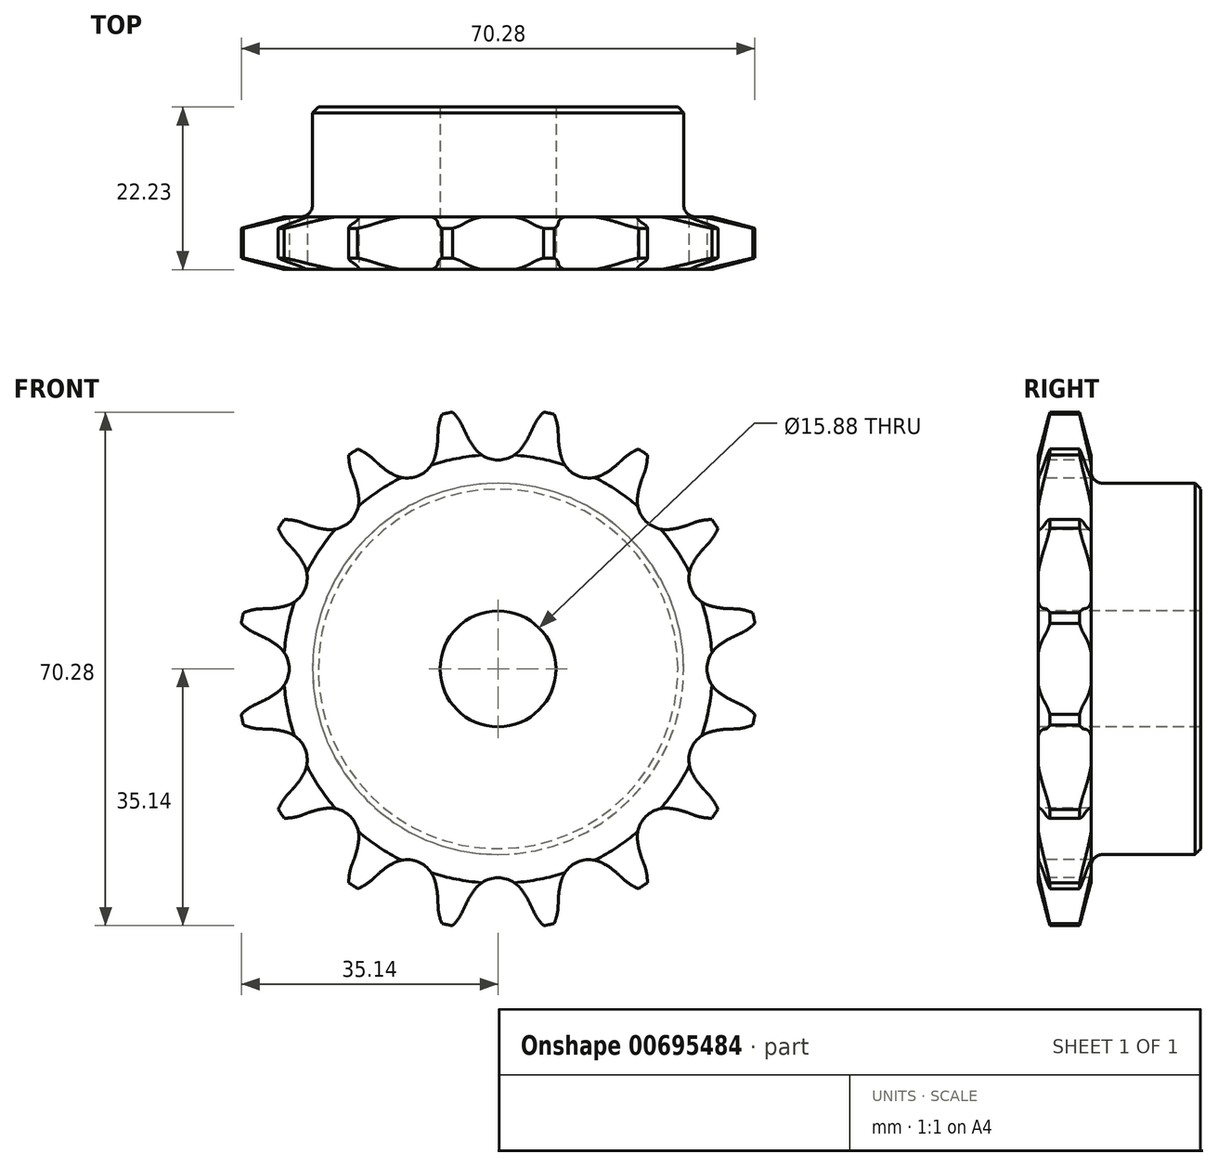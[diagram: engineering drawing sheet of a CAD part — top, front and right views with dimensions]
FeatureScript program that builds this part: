
annotation { "Feature Type Name" : "Feature", "Feature Type Description" : "" }
export const myFeature = defineFeature(function(context is Context, id is Id, definition is map)
    precondition{}
    {
        {
            var Q0;
            Q0=qCreatedBy(makeId("Right.planeOp"),FACE);
            var sketch = newSketch(context, id + "F0", { "sketchPlane" : qUnion([Q0])});
            skLineSegment(sketch, "E0", {"start": v(0, 0) * mm, "end": v(20.66, 0) * mm, "construction": true});
            skLineSegment(sketch, "E1.bottom", {"start": v(-1.57, 35.69) * mm, "end": v(5.65, 35.69) * mm});
            skLineSegment(sketch, "E1.top", {"start": v(-1.57, 7.94) * mm, "end": v(5.65, 7.94) * mm});
            skLineSegment(sketch, "E1.left", {"start": v(-1.57, 35.69) * mm, "end": v(-1.57, 7.94) * mm});
            skLineSegment(sketch, "E1.right", {"start": v(5.65, 35.69) * mm, "end": v(5.65, 7.94) * mm});
            skLineSegment(sketch, "E2.bottom", {"start": v(-1.57, 7.94) * mm, "end": v(20.66, 7.94) * mm});
            skLineSegment(sketch, "E2.top", {"start": v(-1.57, 25.4) * mm, "end": v(20.66, 25.4) * mm});
            skLineSegment(sketch, "E2.left", {"start": v(-1.57, 7.94) * mm, "end": v(-1.57, 25.4) * mm});
            skLineSegment(sketch, "E2.right", {"start": v(20.66, 7.94) * mm, "end": v(20.66, 25.4) * mm});
            skLineSegment(sketch, "E3.MirrorCS", {"start": v(-1.57, -7.94) * mm, "end": v(5.65, -7.94) * mm});
            skLineSegment(sketch, "E4.MirrorCS", {"start": v(20.66, -7.94) * mm, "end": v(20.66, -25.4) * mm});
            skLineSegment(sketch, "E5.MirrorCS", {"start": v(-1.57, -7.94) * mm, "end": v(20.66, -7.94) * mm});
            skLineSegment(sketch, "E6.MirrorCS", {"start": v(-1.57, -35.69) * mm, "end": v(5.65, -35.69) * mm});
            skLineSegment(sketch, "E7.MirrorCS", {"start": v(-1.57, -7.94) * mm, "end": v(-1.57, -25.4) * mm});
            skLineSegment(sketch, "E8.MirrorCS", {"start": v(-1.57, -25.4) * mm, "end": v(20.66, -25.4) * mm});
            skLineSegment(sketch, "E9.MirrorCS", {"start": v(5.65, -35.69) * mm, "end": v(5.65, -7.94) * mm});
            skLineSegment(sketch, "E10.MirrorCS", {"start": v(-1.57, -35.69) * mm, "end": v(-1.57, -7.94) * mm});
            skSolve(sketch);
        }
        {
            var Q0;
            {var subQ0=sQuery(id+"F0.wireOp",EDGE,"E1.bottom");Q0=makeQuery(id+"F0.imprint","IMPRINT",FACE,{"disambiguationData":[TD([[makeQuery(id+"F0.imprint","IMPRINT",EDGE,{"derivedFrom":subQ0}),-1.0]])]});}
            var Q1;
            {var subQ0=sQuery(id+"F0.wireOp",EDGE,"E1.top");Q1=makeQuery(id+"F0.imprint","IMPRINT",FACE,{"disambiguationData":[TD([[makeQuery(id+"F0.imprint","IMPRINT",EDGE,{"derivedFrom":subQ0}),1.0]])]});}
            var Q2;
            {var subQ0=sQuery(id+"F0.wireOp",EDGE,"E2.bottom");Q2=makeQuery(id+"F0.imprint","IMPRINT",FACE,{"disambiguationData":[TD([[makeQuery(id+"F0.imprint","IMPRINT",EDGE,{"derivedFrom":subQ0}),1.0]])]});}
            var Q3;
            Q3=sQuery(id+"F0.wireOp",EDGE,"E0");
            revolve(context, id + "F1", {"surfaceOperationType" : NewSurfaceOperationType.NEW, "entities" : qUnion([Q0, Q1, Q2]), "axis" : qUnion([Q3]), "revolveType" : RevolveType.FULL});
        }
        {
            var Q0;
            Q0=makeQuery(id+"F1.opRevolve","SWEPT_EDGE",EDGE,{"disambiguationData":[OSD([sQuery(id+"F0.wireOp",EDGE,"E1.right"),sQuery(id+"F0.wireOp",EDGE,"E2.top")])]});
            fillet(context, id + "F2", {"entities" : qUnion([Q0]), "tangentPropagation" : true, "radius" : 1.59 * mm, "defaultsChanged" : false, "vertexSettings" : [], "allowEdgeOverflow" : false});
        }
        {
            var Q0;
            Q0=makeQuery(id+"F1.opRevolve","SWEPT_EDGE",EDGE,{"disambiguationData":[OSD([sQuery(id+"F0.wireOp",EDGE,"E2.top"),sQuery(id+"F0.wireOp",EDGE,"E2.right")])]});
            chamfer(context, id + "F3", {"entities" : qUnion([Q0]), "width" : 0.8 * mm, "tangentPropagation" : true});
        }
        {
            var Q0;
            Q0=makeQuery(id+"F1.opRevolve","SWEPT_EDGE",EDGE,{"disambiguationData":[OSD([sQuery(id+"F0.wireOp",EDGE,"E1.bottom"),sQuery(id+"F0.wireOp",EDGE,"E1.left")])]});
            var Q1;
            Q1=makeQuery(id+"F1.opRevolve","SWEPT_EDGE",EDGE,{"disambiguationData":[OSD([sQuery(id+"F0.wireOp",EDGE,"E1.bottom"),sQuery(id+"F0.wireOp",EDGE,"E1.right")])]});
            chamfer(context, id + "F4", {"entities" : qUnion([Q0, Q1]), "chamferType" : ChamferType.TWO_OFFSETS, "width1" : 6.35 * mm, "oppositeDirection" : false, "width2" : 1.57 * mm, "tangentPropagation" : true});
        }
        {
            var Q0;
            Q0=makeQuery(id+"F1.opRevolve","SWEPT_FACE",FACE,{"disambiguationData":[OSD([sQuery(id+"F0.wireOp",EDGE,"E1.left")])]});
            var sketch = newSketch(context, id + "F5", { "sketchPlane" : qUnion([Q0])});
            skCircle(sketch, "E11", {"center": v(0, 0) * mm, "radius": 32.55 * mm, "construction": true});
            skLineSegment(sketch, "E12", {"start": v(0, 0) * mm, "end": v(0, 32.55) * mm, "construction": true});
            skLineSegment(sketch, "E13", {"start": v(0, 32.55) * mm, "end": v(42.62, 32.55) * mm, "construction": true});
            skLineSegment(sketch, "E14", {"start": v(0, 32.55) * mm, "end": v(5, 36.56) * mm, "construction": true});
            skLineSegment(sketch, "E15", {"start": v(5, 36.56) * mm, "end": v(-4.46, 32.3) * mm, "construction": true});
            skLineSegment(sketch, "E16", {"start": v(-4.46, 32.3) * mm, "end": v(-4.82, 33.1) * mm});
            skLineSegment(sketch, "E17", {"start": v(0, 0) * mm, "end": v(-7.13, 35.85) * mm, "construction": true});
            skArc(sketch, "E18", {"start": v(-7.13, 35.85) * mm, "mid": v(-15.87, 26.15) * mm, "end": v(-4.82, 33.1) * mm, "construction": true});
            skArc(sketch, "E19", {"start": v(-4.82, 33.1) * mm, "mid": v(-5.78, 34.63) * mm, "end": v(-7.13, 35.85) * mm});
            skLineSegment(sketch, "E20", {"start": v(5.43, 10.36) * mm, "end": v(-4.82, 33.1) * mm, "construction": true});
            skArc(sketch, "E21", {"start": v(-4.46, 32.3) * mm, "mid": v(-3.84, 31.14) * mm, "end": v(-3.1, 30.07) * mm});
            skArc(sketch, "E22", {"start": v(-3.1, 30.07) * mm, "mid": v(13.81, 42) * mm, "end": v(-4.43, 32.25) * mm, "construction": true});
            skArc(sketch, "E23.MirrorCS", {"start": v(4.82, 33.1) * mm, "mid": v(5.78, 34.63) * mm, "end": v(7.13, 35.85) * mm});
            skLineSegment(sketch, "E24.MirrorCS", {"start": v(4.46, 32.3) * mm, "end": v(4.82, 33.1) * mm});
            skArc(sketch, "E25.MirrorCS", {"start": v(4.46, 32.3) * mm, "mid": v(3.84, 31.14) * mm, "end": v(3.1, 30.07) * mm});
            skLineSegment(sketch, "E26", {"start": v(3.1, 30.07) * mm, "end": v(3.1, 30.07) * mm});
            skArc(sketch, "E27", {"start": v(-3.1, 30.07) * mm, "mid": v(0, 28.59) * mm, "end": v(3.1, 30.07) * mm});
            skArc(sketch, "E28", {"start": v(3.1, 30.07) * mm, "mid": v(0, 36.51) * mm, "end": v(-3.1, 30.07) * mm, "construction": true});
            skArc(sketch, "E29.1.0", {"start": v(-17.12, 28.74) * mm, "mid": v(-18.6, 29.79) * mm, "end": v(-20.3, 30.4) * mm});
            skLineSegment(sketch, "E29.1.1", {"start": v(-16.48, 28.14) * mm, "end": v(-17.12, 28.74) * mm});
            skArc(sketch, "E29.1.2", {"start": v(-16.48, 28.14) * mm, "mid": v(-15.47, 27.3) * mm, "end": v(-14.36, 26.6) * mm});
            skArc(sketch, "E29.1.3", {"start": v(-14.36, 26.6) * mm, "mid": v(-10.94, 26.41) * mm, "end": v(-8.65, 28.96) * mm});
            skArc(sketch, "E29.1.4", {"start": v(-8.24, 31.55) * mm, "mid": v(-8.37, 30.24) * mm, "end": v(-8.65, 28.96) * mm});
            skLineSegment(sketch, "E29.1.5", {"start": v(-8.24, 31.55) * mm, "end": v(-8.22, 32.42) * mm});
            skArc(sketch, "E29.1.6", {"start": v(-8.22, 32.42) * mm, "mid": v(-7.91, 34.21) * mm, "end": v(-7.13, 35.85) * mm});
            skArc(sketch, "E29.2.0", {"start": v(-26.8, 20) * mm, "mid": v(-28.58, 20.4) * mm, "end": v(-30.4, 20.3) * mm});
            skLineSegment(sketch, "E29.2.1", {"start": v(-26, 19.69) * mm, "end": v(-26.8, 20) * mm});
            skArc(sketch, "E29.2.2", {"start": v(-26, 19.69) * mm, "mid": v(-24.74, 19.3) * mm, "end": v(-23.45, 19.08) * mm});
            skArc(sketch, "E29.2.3", {"start": v(-23.45, 19.08) * mm, "mid": v(-20.21, 20.21) * mm, "end": v(-19.08, 23.45) * mm});
            skArc(sketch, "E29.2.4", {"start": v(-19.69, 26) * mm, "mid": v(-19.3, 24.74) * mm, "end": v(-19.08, 23.45) * mm});
            skLineSegment(sketch, "E29.2.5", {"start": v(-19.69, 26) * mm, "end": v(-20, 26.8) * mm});
            skArc(sketch, "E29.2.6", {"start": v(-20, 26.8) * mm, "mid": v(-20.4, 28.58) * mm, "end": v(-20.3, 30.4) * mm});
            skArc(sketch, "E29.3.0", {"start": v(-32.42, 8.22) * mm, "mid": v(-34.21, 7.91) * mm, "end": v(-35.85, 7.13) * mm});
            skLineSegment(sketch, "E29.3.1", {"start": v(-31.55, 8.24) * mm, "end": v(-32.42, 8.22) * mm});
            skArc(sketch, "E29.3.2", {"start": v(-31.55, 8.24) * mm, "mid": v(-30.24, 8.37) * mm, "end": v(-28.96, 8.65) * mm});
            skArc(sketch, "E29.3.3", {"start": v(-28.96, 8.65) * mm, "mid": v(-26.41, 10.94) * mm, "end": v(-26.6, 14.36) * mm});
            skArc(sketch, "E29.3.4", {"start": v(-28.14, 16.48) * mm, "mid": v(-27.3, 15.47) * mm, "end": v(-26.6, 14.36) * mm});
            skLineSegment(sketch, "E29.3.5", {"start": v(-28.14, 16.48) * mm, "end": v(-28.74, 17.12) * mm});
            skArc(sketch, "E29.3.6", {"start": v(-28.74, 17.12) * mm, "mid": v(-29.79, 18.6) * mm, "end": v(-30.4, 20.3) * mm});
            skArc(sketch, "E29.4.0", {"start": v(-33.1, -4.82) * mm, "mid": v(-34.63, -5.78) * mm, "end": v(-35.85, -7.13) * mm});
            skLineSegment(sketch, "E29.4.1", {"start": v(-32.3, -4.46) * mm, "end": v(-33.1, -4.82) * mm});
            skArc(sketch, "E29.4.2", {"start": v(-32.3, -4.46) * mm, "mid": v(-31.14, -3.84) * mm, "end": v(-30.07, -3.1) * mm});
            skArc(sketch, "E29.4.3", {"start": v(-30.07, -3.1) * mm, "mid": v(-28.59, 0) * mm, "end": v(-30.07, 3.1) * mm});
            skArc(sketch, "E29.4.4", {"start": v(-32.3, 4.46) * mm, "mid": v(-31.14, 3.84) * mm, "end": v(-30.07, 3.1) * mm});
            skLineSegment(sketch, "E29.4.5", {"start": v(-32.3, 4.46) * mm, "end": v(-33.1, 4.82) * mm});
            skArc(sketch, "E29.4.6", {"start": v(-33.1, 4.82) * mm, "mid": v(-34.63, 5.78) * mm, "end": v(-35.85, 7.13) * mm});
            skArc(sketch, "E29.5.0", {"start": v(-28.74, -17.12) * mm, "mid": v(-29.79, -18.6) * mm, "end": v(-30.4, -20.3) * mm});
            skLineSegment(sketch, "E29.5.1", {"start": v(-28.14, -16.48) * mm, "end": v(-28.74, -17.12) * mm});
            skArc(sketch, "E29.5.2", {"start": v(-28.14, -16.48) * mm, "mid": v(-27.3, -15.47) * mm, "end": v(-26.6, -14.36) * mm});
            skArc(sketch, "E29.5.3", {"start": v(-26.6, -14.36) * mm, "mid": v(-26.41, -10.94) * mm, "end": v(-28.96, -8.65) * mm});
            skArc(sketch, "E29.5.4", {"start": v(-31.55, -8.24) * mm, "mid": v(-30.24, -8.37) * mm, "end": v(-28.96, -8.65) * mm});
            skLineSegment(sketch, "E29.5.5", {"start": v(-31.55, -8.24) * mm, "end": v(-32.42, -8.22) * mm});
            skArc(sketch, "E29.5.6", {"start": v(-32.42, -8.22) * mm, "mid": v(-34.21, -7.91) * mm, "end": v(-35.85, -7.13) * mm});
            skArc(sketch, "E29.6.0", {"start": v(-20, -26.8) * mm, "mid": v(-20.4, -28.58) * mm, "end": v(-20.3, -30.4) * mm});
            skLineSegment(sketch, "E29.6.1", {"start": v(-19.69, -26) * mm, "end": v(-20, -26.8) * mm});
            skArc(sketch, "E29.6.2", {"start": v(-19.69, -26) * mm, "mid": v(-19.3, -24.74) * mm, "end": v(-19.08, -23.45) * mm});
            skArc(sketch, "E29.6.3", {"start": v(-19.08, -23.45) * mm, "mid": v(-20.21, -20.21) * mm, "end": v(-23.45, -19.08) * mm});
            skArc(sketch, "E29.6.4", {"start": v(-26, -19.69) * mm, "mid": v(-24.74, -19.3) * mm, "end": v(-23.45, -19.08) * mm});
            skLineSegment(sketch, "E29.6.5", {"start": v(-26, -19.69) * mm, "end": v(-26.8, -20) * mm});
            skArc(sketch, "E29.6.6", {"start": v(-26.8, -20) * mm, "mid": v(-28.58, -20.4) * mm, "end": v(-30.4, -20.3) * mm});
            skArc(sketch, "E29.7.0", {"start": v(-8.22, -32.42) * mm, "mid": v(-7.91, -34.21) * mm, "end": v(-7.13, -35.85) * mm});
            skLineSegment(sketch, "E29.7.1", {"start": v(-8.24, -31.55) * mm, "end": v(-8.22, -32.42) * mm});
            skArc(sketch, "E29.7.2", {"start": v(-8.24, -31.55) * mm, "mid": v(-8.37, -30.24) * mm, "end": v(-8.65, -28.96) * mm});
            skArc(sketch, "E29.7.3", {"start": v(-8.65, -28.96) * mm, "mid": v(-10.94, -26.41) * mm, "end": v(-14.36, -26.6) * mm});
            skArc(sketch, "E29.7.4", {"start": v(-16.48, -28.14) * mm, "mid": v(-15.47, -27.3) * mm, "end": v(-14.36, -26.6) * mm});
            skLineSegment(sketch, "E29.7.5", {"start": v(-16.48, -28.14) * mm, "end": v(-17.12, -28.74) * mm});
            skArc(sketch, "E29.7.6", {"start": v(-17.12, -28.74) * mm, "mid": v(-18.6, -29.79) * mm, "end": v(-20.3, -30.4) * mm});
            skArc(sketch, "E29.8.0", {"start": v(4.82, -33.1) * mm, "mid": v(5.78, -34.63) * mm, "end": v(7.13, -35.85) * mm});
            skLineSegment(sketch, "E29.8.1", {"start": v(4.46, -32.3) * mm, "end": v(4.82, -33.1) * mm});
            skArc(sketch, "E29.8.2", {"start": v(4.46, -32.3) * mm, "mid": v(3.84, -31.14) * mm, "end": v(3.1, -30.07) * mm});
            skArc(sketch, "E29.8.3", {"start": v(3.1, -30.07) * mm, "mid": v(0, -28.59) * mm, "end": v(-3.1, -30.07) * mm});
            skArc(sketch, "E29.8.4", {"start": v(-4.46, -32.3) * mm, "mid": v(-3.84, -31.14) * mm, "end": v(-3.1, -30.07) * mm});
            skLineSegment(sketch, "E29.8.5", {"start": v(-4.46, -32.3) * mm, "end": v(-4.82, -33.1) * mm});
            skArc(sketch, "E29.8.6", {"start": v(-4.82, -33.1) * mm, "mid": v(-5.78, -34.63) * mm, "end": v(-7.13, -35.85) * mm});
            skArc(sketch, "E29.9.0", {"start": v(17.12, -28.74) * mm, "mid": v(18.6, -29.79) * mm, "end": v(20.3, -30.4) * mm});
            skLineSegment(sketch, "E29.9.1", {"start": v(16.48, -28.14) * mm, "end": v(17.12, -28.74) * mm});
            skArc(sketch, "E29.9.2", {"start": v(16.48, -28.14) * mm, "mid": v(15.47, -27.3) * mm, "end": v(14.36, -26.6) * mm});
            skArc(sketch, "E29.9.3", {"start": v(14.36, -26.6) * mm, "mid": v(10.94, -26.41) * mm, "end": v(8.65, -28.96) * mm});
            skArc(sketch, "E29.9.4", {"start": v(8.24, -31.55) * mm, "mid": v(8.37, -30.24) * mm, "end": v(8.65, -28.96) * mm});
            skLineSegment(sketch, "E29.9.5", {"start": v(8.24, -31.55) * mm, "end": v(8.22, -32.42) * mm});
            skArc(sketch, "E29.9.6", {"start": v(8.22, -32.42) * mm, "mid": v(7.91, -34.21) * mm, "end": v(7.13, -35.85) * mm});
            skArc(sketch, "E29.10.0", {"start": v(26.8, -20) * mm, "mid": v(28.58, -20.4) * mm, "end": v(30.4, -20.3) * mm});
            skLineSegment(sketch, "E29.10.1", {"start": v(26, -19.69) * mm, "end": v(26.8, -20) * mm});
            skArc(sketch, "E29.10.2", {"start": v(26, -19.69) * mm, "mid": v(24.74, -19.3) * mm, "end": v(23.45, -19.08) * mm});
            skArc(sketch, "E29.10.3", {"start": v(23.45, -19.08) * mm, "mid": v(20.21, -20.21) * mm, "end": v(19.08, -23.45) * mm});
            skArc(sketch, "E29.10.4", {"start": v(19.69, -26) * mm, "mid": v(19.3, -24.74) * mm, "end": v(19.08, -23.45) * mm});
            skLineSegment(sketch, "E29.10.5", {"start": v(19.69, -26) * mm, "end": v(20, -26.8) * mm});
            skArc(sketch, "E29.10.6", {"start": v(20, -26.8) * mm, "mid": v(20.4, -28.58) * mm, "end": v(20.3, -30.4) * mm});
            skArc(sketch, "E29.11.0", {"start": v(32.42, -8.22) * mm, "mid": v(34.21, -7.91) * mm, "end": v(35.85, -7.13) * mm});
            skLineSegment(sketch, "E29.11.1", {"start": v(31.55, -8.24) * mm, "end": v(32.42, -8.22) * mm});
            skArc(sketch, "E29.11.2", {"start": v(31.55, -8.24) * mm, "mid": v(30.24, -8.37) * mm, "end": v(28.96, -8.65) * mm});
            skArc(sketch, "E29.11.3", {"start": v(28.96, -8.65) * mm, "mid": v(26.41, -10.94) * mm, "end": v(26.6, -14.36) * mm});
            skArc(sketch, "E29.11.4", {"start": v(28.14, -16.48) * mm, "mid": v(27.3, -15.47) * mm, "end": v(26.6, -14.36) * mm});
            skLineSegment(sketch, "E29.11.5", {"start": v(28.14, -16.48) * mm, "end": v(28.74, -17.12) * mm});
            skArc(sketch, "E29.11.6", {"start": v(28.74, -17.12) * mm, "mid": v(29.79, -18.6) * mm, "end": v(30.4, -20.3) * mm});
            skArc(sketch, "E29.12.0", {"start": v(33.1, 4.82) * mm, "mid": v(34.63, 5.78) * mm, "end": v(35.85, 7.13) * mm});
            skLineSegment(sketch, "E29.12.1", {"start": v(32.3, 4.46) * mm, "end": v(33.1, 4.82) * mm});
            skArc(sketch, "E29.12.2", {"start": v(32.3, 4.46) * mm, "mid": v(31.14, 3.84) * mm, "end": v(30.07, 3.1) * mm});
            skArc(sketch, "E29.12.3", {"start": v(30.07, 3.1) * mm, "mid": v(28.59, 0) * mm, "end": v(30.07, -3.1) * mm});
            skArc(sketch, "E29.12.4", {"start": v(32.3, -4.46) * mm, "mid": v(31.14, -3.84) * mm, "end": v(30.07, -3.1) * mm});
            skLineSegment(sketch, "E29.12.5", {"start": v(32.3, -4.46) * mm, "end": v(33.1, -4.82) * mm});
            skArc(sketch, "E29.12.6", {"start": v(33.1, -4.82) * mm, "mid": v(34.63, -5.78) * mm, "end": v(35.85, -7.13) * mm});
            skArc(sketch, "E29.13.0", {"start": v(28.74, 17.12) * mm, "mid": v(29.79, 18.6) * mm, "end": v(30.4, 20.3) * mm});
            skLineSegment(sketch, "E29.13.1", {"start": v(28.14, 16.48) * mm, "end": v(28.74, 17.12) * mm});
            skArc(sketch, "E29.13.2", {"start": v(28.14, 16.48) * mm, "mid": v(27.3, 15.47) * mm, "end": v(26.6, 14.36) * mm});
            skArc(sketch, "E29.13.3", {"start": v(26.6, 14.36) * mm, "mid": v(26.41, 10.94) * mm, "end": v(28.96, 8.65) * mm});
            skArc(sketch, "E29.13.4", {"start": v(31.55, 8.24) * mm, "mid": v(30.24, 8.37) * mm, "end": v(28.96, 8.65) * mm});
            skLineSegment(sketch, "E29.13.5", {"start": v(31.55, 8.24) * mm, "end": v(32.42, 8.22) * mm});
            skArc(sketch, "E29.13.6", {"start": v(32.42, 8.22) * mm, "mid": v(34.21, 7.91) * mm, "end": v(35.85, 7.13) * mm});
            skArc(sketch, "E29.14.0", {"start": v(20, 26.8) * mm, "mid": v(20.4, 28.58) * mm, "end": v(20.3, 30.4) * mm});
            skLineSegment(sketch, "E29.14.1", {"start": v(19.69, 26) * mm, "end": v(20, 26.8) * mm});
            skArc(sketch, "E29.14.2", {"start": v(19.69, 26) * mm, "mid": v(19.3, 24.74) * mm, "end": v(19.08, 23.45) * mm});
            skArc(sketch, "E29.14.3", {"start": v(19.08, 23.45) * mm, "mid": v(20.21, 20.21) * mm, "end": v(23.45, 19.08) * mm});
            skArc(sketch, "E29.14.4", {"start": v(26, 19.69) * mm, "mid": v(24.74, 19.3) * mm, "end": v(23.45, 19.08) * mm});
            skLineSegment(sketch, "E29.14.5", {"start": v(26, 19.69) * mm, "end": v(26.8, 20) * mm});
            skArc(sketch, "E29.14.6", {"start": v(26.8, 20) * mm, "mid": v(28.58, 20.4) * mm, "end": v(30.4, 20.3) * mm});
            skArc(sketch, "E29.15.0", {"start": v(8.22, 32.42) * mm, "mid": v(7.91, 34.21) * mm, "end": v(7.13, 35.85) * mm});
            skLineSegment(sketch, "E29.15.1", {"start": v(8.24, 31.55) * mm, "end": v(8.22, 32.42) * mm});
            skArc(sketch, "E29.15.2", {"start": v(8.24, 31.55) * mm, "mid": v(8.37, 30.24) * mm, "end": v(8.65, 28.96) * mm});
            skArc(sketch, "E29.15.3", {"start": v(8.65, 28.96) * mm, "mid": v(10.94, 26.41) * mm, "end": v(14.36, 26.6) * mm});
            skArc(sketch, "E29.15.4", {"start": v(16.48, 28.14) * mm, "mid": v(15.47, 27.3) * mm, "end": v(14.36, 26.6) * mm});
            skLineSegment(sketch, "E29.15.5", {"start": v(16.48, 28.14) * mm, "end": v(17.12, 28.74) * mm});
            skArc(sketch, "E29.15.6", {"start": v(17.12, 28.74) * mm, "mid": v(18.6, 29.79) * mm, "end": v(20.3, 30.4) * mm});
            skSolve(sketch);
        }
        {
            var Q0;
            Q0 = qSketchRegion(id + "F5", true);
            extrude(context, id + "F6", {"entities" : qUnion([Q0]), "operationType" : NewBodyOperationType.INTERSECT, "endBound" : BoundingType.THROUGH_ALL, "oppositeDirection" : true, "depth" : 25.4 * mm, "offsetDistance" : 25.4 * mm});
        }
    });
